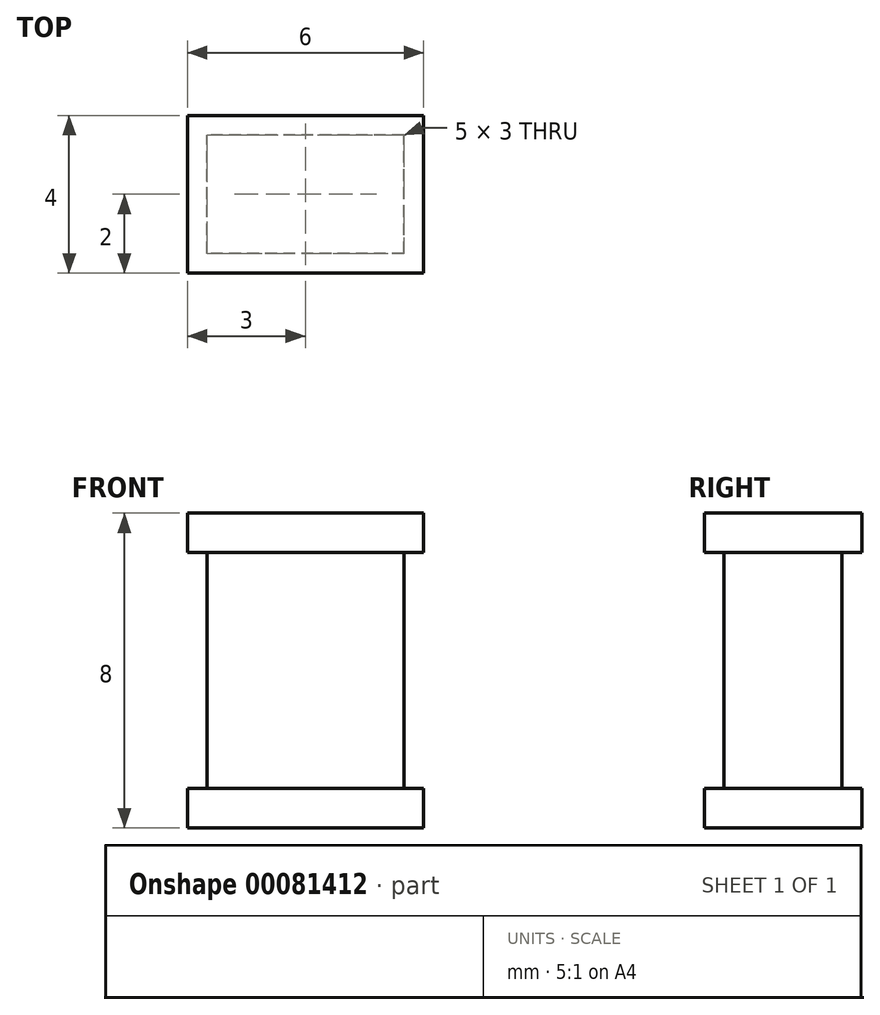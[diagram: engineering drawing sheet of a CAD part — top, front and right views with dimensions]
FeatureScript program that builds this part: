
annotation { "Feature Type Name" : "Feature", "Feature Type Description" : "" }
export const myFeature = defineFeature(function(context is Context, id is Id, definition is map)
    precondition{}
    {
        {
            var Q0;
            Q0=qCreatedBy(makeId("Top.planeOp"),FACE);
            var sketch = newSketch(context, id + "F0", { "sketchPlane" : qUnion([Q0])});
            skLineSegment(sketch, "E0.bottom", {"start": v(2.5, -1.5) * mm, "end": v(-2.5, -1.5) * mm});
            skLineSegment(sketch, "E0.top", {"start": v(2.5, 1.5) * mm, "end": v(-2.5, 1.5) * mm});
            skLineSegment(sketch, "E0.left", {"start": v(2.5, -1.5) * mm, "end": v(2.5, 1.5) * mm});
            skLineSegment(sketch, "E0.right", {"start": v(-2.5, -1.5) * mm, "end": v(-2.5, 1.5) * mm});
            skPoint(sketch, "E0.middle", {"position": v(0, 0) * mm});
            skSolve(sketch);
        }
        {
            var Q0;
            Q0=makeQuery(id+"F0.imprint","IMPRINT",FACE,{"disambiguationData":[TD([[makeQuery(id+"F0.imprint","IMPRINT",EDGE,{"derivedFrom":sQuery(id+"F0.wireOp",EDGE,"E0.bottom")}),-1.0]])]});
            extrude(context, id + "F1", {"entities" : qUnion([Q0]), "depth" : 6 * mm});
        }
        {
            var Q0;
            Q0=makeQuery(id+"F1.opExtrude","CAP_FACE",FACE,{"disambiguationData":[OSD([sQuery(id+"F0.wireOp",EDGE,"E0.bottom"),sQuery(id+"F0.wireOp",EDGE,"E0.top"),sQuery(id+"F0.wireOp",EDGE,"E0.left"),sQuery(id+"F0.wireOp",EDGE,"E0.right")])],"isStart":false});
            var sketch = newSketch(context, id + "F2", { "sketchPlane" : qUnion([Q0])});
            skLineSegment(sketch, "E1.bottom", {"start": v(3, -2) * mm, "end": v(-3, -2) * mm});
            skLineSegment(sketch, "E1.top", {"start": v(3, 2) * mm, "end": v(-3, 2) * mm});
            skLineSegment(sketch, "E1.left", {"start": v(3, -2) * mm, "end": v(3, 2) * mm});
            skLineSegment(sketch, "E1.right", {"start": v(-3, -2) * mm, "end": v(-3, 2) * mm});
            skPoint(sketch, "E1.middle", {"position": v(0, 0) * mm});
            skSolve(sketch);
        }
        {
            var Q0;
            Q0 = qSketchRegion(id + "F2", true);
            extrude(context, id + "F3", {"entities" : qUnion([Q0]), "operationType" : NewBodyOperationType.ADD, "depth" : 1 * mm});
        }
        {
            var Q0;
            Q0=makeQuery(id+"F1.opExtrude","CAP_FACE",FACE,{"disambiguationData":[OSD([sQuery(id+"F0.wireOp",EDGE,"E0.bottom"),sQuery(id+"F0.wireOp",EDGE,"E0.top"),sQuery(id+"F0.wireOp",EDGE,"E0.left"),sQuery(id+"F0.wireOp",EDGE,"E0.right")])],"isStart":true});
            var sketch = newSketch(context, id + "F4", { "sketchPlane" : qUnion([Q0])});
            skLineSegment(sketch, "E2.0", {"start": v(3, -2) * mm, "end": v(-3, -2) * mm, "construction": true});
            skLineSegment(sketch, "E3.bottom", {"start": v(-3, -2) * mm, "end": v(3, -2) * mm, "construction": true});
            skLineSegment(sketch, "E3.top", {"start": v(-3, 2) * mm, "end": v(3, 2) * mm, "construction": true});
            skLineSegment(sketch, "E3.left", {"start": v(-3, -2) * mm, "end": v(-3, 2) * mm, "construction": true});
            skLineSegment(sketch, "E3.right", {"start": v(3, -2) * mm, "end": v(3, 2) * mm, "construction": true});
            skPoint(sketch, "E3.middle", {"position": v(0, 0) * mm});
            skLineSegment(sketch, "E4.bottom", {"start": v(-3, -2) * mm, "end": v(3, -2) * mm});
            skLineSegment(sketch, "E4.top", {"start": v(-3, 2) * mm, "end": v(3, 2) * mm});
            skLineSegment(sketch, "E4.left", {"start": v(-3, -2) * mm, "end": v(-3, 2) * mm});
            skLineSegment(sketch, "E4.right", {"start": v(3, -2) * mm, "end": v(3, 2) * mm});
            skSolve(sketch);
        }
        {
            var Q0;
            Q0 = qSketchRegion(id + "F4", true);
            extrude(context, id + "F5", {"entities" : qUnion([Q0]), "operationType" : NewBodyOperationType.ADD, "depth" : 1 * mm});
        }
    });
